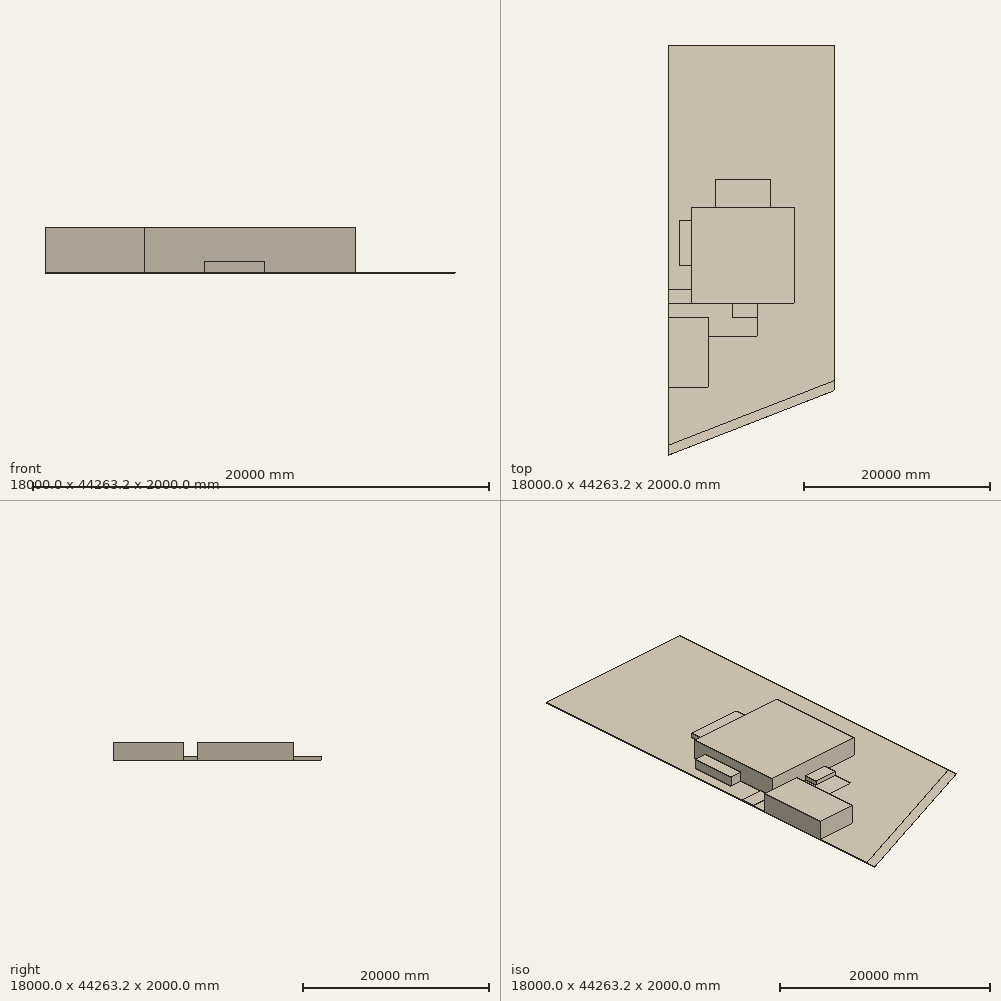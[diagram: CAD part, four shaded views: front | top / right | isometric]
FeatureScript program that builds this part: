
annotation { "Feature Type Name" : "Feature", "Feature Type Description" : "" }
export const myFeature = defineFeature(function(context is Context, id is Id, definition is map)
    precondition{}
    {
        {
            var Q0;
            Q0=qCreatedBy(makeId("Top.planeOp"),FACE);
            var sketch = newSketch(context, id + "F0", { "sketchPlane" : qUnion([Q0])});
            skLineSegment(sketch, "E0", {"start": v(0, 0) * mm, "end": v(18000, 0) * mm});
            skLineSegment(sketch, "E1", {"start": v(18000, 0) * mm, "end": v(18000, -37248.55) * mm});
            skLineSegment(sketch, "E2", {"start": v(0, 0) * mm, "end": v(0, -44263.25) * mm});
            skLineSegment(sketch, "E3", {"start": v(0, -44263.25) * mm, "end": v(18000, -37248.55) * mm});
            skLineSegment(sketch, "E4.bottom", {"start": v(2500, -17500) * mm, "end": v(13600, -17500) * mm});
            skLineSegment(sketch, "E4.top", {"start": v(2500, -27890) * mm, "end": v(13600, -27890) * mm});
            skLineSegment(sketch, "E4.left", {"start": v(2500, -17500) * mm, "end": v(2500, -27890) * mm});
            skLineSegment(sketch, "E4.right", {"start": v(13600, -17500) * mm, "end": v(13600, -27890) * mm});
            skLineSegment(sketch, "E5.bottom", {"start": v(4360, -29390) * mm, "end": v(0, -29390) * mm});
            skLineSegment(sketch, "E5.top", {"start": v(4360, -36890) * mm, "end": v(0, -36890) * mm});
            skLineSegment(sketch, "E5.left", {"start": v(4360, -29390) * mm, "end": v(4360, -36890) * mm});
            skLineSegment(sketch, "E5.right", {"start": v(0, -29390) * mm, "end": v(0, -36890) * mm});
            skLineSegment(sketch, "E6", {"start": v(0, -43190) * mm, "end": v(18000, -36175.3) * mm});
            skLineSegment(sketch, "E7", {"start": v(13600, -27890) * mm, "end": v(13600, -37890) * mm, "construction": true});
            skSolve(sketch);
        }
        {
            var Q0;
            {var subQ1=sQuery(id+"F0.wireOp",EDGE,"E0");Q0=makeQuery(id+"F0.imprint","IMPRINT",FACE,{"disambiguationData":[TD([[makeQuery(id+"F0.imprint","IMPRINT",EDGE,{"derivedFrom":subQ1}),-1.0]])]});}
            var sketch = newSketch(context, id + "F1", { "sketchPlane" : qUnion([Q0])});
            skLineSegment(sketch, "E8", {"start": v(0, 0) * mm, "end": v(18000, 0) * mm});
            skLineSegment(sketch, "E9", {"start": v(18000, 0) * mm, "end": v(18000, -37248.55) * mm});
            skLineSegment(sketch, "E10", {"start": v(18000, -37248.55) * mm, "end": v(0, -44263.25) * mm});
            skLineSegment(sketch, "E11", {"start": v(0, -44263.25) * mm, "end": v(0, 0) * mm});
            skSolve(sketch);
        }
        {
            var Q0;
            {var subQ1=sQuery(id+"F1.wireOp",EDGE,"E8");Q0=makeQuery(id+"F1.imprint","IMPRINT",FACE,{"disambiguationData":[TD([[makeQuery(id+"F1.imprint","IMPRINT",EDGE,{"derivedFrom":subQ1}),-1.0]])]});}
            var sketch = newSketch(context, id + "F2", { "sketchPlane" : qUnion([Q0])});
            skLineSegment(sketch, "E12.bottom", {"start": v(7000, -27890) * mm, "end": v(9600, -27890) * mm});
            skLineSegment(sketch, "E12.top", {"start": v(7000, -29340) * mm, "end": v(9600, -29340) * mm});
            skLineSegment(sketch, "E12.left", {"start": v(7000, -27890) * mm, "end": v(7000, -29340) * mm});
            skLineSegment(sketch, "E12.right", {"start": v(9600, -27890) * mm, "end": v(9600, -29340) * mm});
            skLineSegment(sketch, "E13", {"start": v(8300, -17500) * mm, "end": v(8300, -27890) * mm, "construction": true});
            skLineSegment(sketch, "E14", {"start": v(5660, -42057.52) * mm, "end": v(5660, -36890) * mm});
            skLineSegment(sketch, "E15.bottom", {"start": v(5086.7, -17500) * mm, "end": v(11086.7, -17500) * mm});
            skLineSegment(sketch, "E15.top", {"start": v(5086.7, -14500) * mm, "end": v(11086.7, -14500) * mm});
            skLineSegment(sketch, "E15.left", {"start": v(5086.7, -17500) * mm, "end": v(5086.7, -14500) * mm});
            skLineSegment(sketch, "E15.right", {"start": v(11086.7, -17500) * mm, "end": v(11086.7, -14500) * mm});
            skLineSegment(sketch, "E16", {"start": v(5660, -42057.52) * mm, "end": v(0, -44263.25) * mm});
            skLineSegment(sketch, "E17", {"start": v(0, -44263.25) * mm, "end": v(0, -36890) * mm});
            skLineSegment(sketch, "E18", {"start": v(0, -36890) * mm, "end": v(4360, -36890) * mm});
            skLineSegment(sketch, "E19", {"start": v(4360, -36890) * mm, "end": v(4360, -29390) * mm});
            skLineSegment(sketch, "E20", {"start": v(4360, -29390) * mm, "end": v(0, -29390) * mm});
            skLineSegment(sketch, "E21", {"start": v(0, -29390) * mm, "end": v(0, -26390) * mm});
            skLineSegment(sketch, "E22", {"start": v(0, -26390) * mm, "end": v(2500, -26390) * mm});
            skLineSegment(sketch, "E23", {"start": v(2500, -26390) * mm, "end": v(2500, -27890) * mm});
            skLineSegment(sketch, "E24", {"start": v(2500, -27890) * mm, "end": v(9600, -27890) * mm});
            skLineSegment(sketch, "E25", {"start": v(4360, -36890) * mm, "end": v(5660, -36890) * mm});
            skLineSegment(sketch, "E26", {"start": v(4360, -31390) * mm, "end": v(9600, -31390) * mm});
            skLineSegment(sketch, "E27", {"start": v(9600, -31390) * mm, "end": v(9600, -29340) * mm});
            skSolve(sketch);
        }
        {
            var Q0;
            {var subQ0=sQuery(id+"F2.wireOp",EDGE,"E18");Q0=makeQuery(id+"F2.imprint","IMPRINT",FACE,{"disambiguationData":[TD([[makeQuery(id+"F2.imprint","IMPRINT",EDGE,{"derivedFrom":subQ0}),1.0]])]});}
            extrude(context, id + "F3", {"entities" : qUnion([Q0]), "depth" : 25 * mm, "offsetDistance" : 25 * mm});
        }
        {
            var Q0;
            {var subQ1=sQuery(id+"F1.wireOp",EDGE,"E8");Q0=makeQuery(id+"F1.imprint","IMPRINT",FACE,{"disambiguationData":[TD([[makeQuery(id+"F1.imprint","IMPRINT",EDGE,{"derivedFrom":subQ1}),-1.0]])]});}
            extrude(context, id + "F4", {"entities" : qUnion([Q0]), "depth" : 25 * mm, "offsetDistance" : 25 * mm});
        }
        {
            var Q0;
            {var subQ0=sQuery(id+"F0.wireOp",EDGE,"E3");Q0=makeQuery(id+"F0.imprint","IMPRINT",FACE,{"disambiguationData":[TD([[makeQuery(id+"F0.imprint","IMPRINT",EDGE,{"derivedFrom":subQ0}),1.0]])]});}
            extrude(context, id + "F5", {"entities" : qUnion([Q0]), "operationType" : NewBodyOperationType.ADD, "depth" : 10 * mm, "offsetDistance" : 25 * mm});
        }
        {
            var Q0;
            Q0=makeQuery(id+"F0.imprint","IMPRINT",FACE,{"disambiguationData":[TD([[makeQuery(id+"F0.imprint","IMPRINT",EDGE,{"derivedFrom":sQuery(id+"F0.wireOp",EDGE,"E4.bottom")}),-1.0]])]});
            var Q1;
            Q1=makeQuery(id+"F0.imprint","IMPRINT",FACE,{"disambiguationData":[TD([[makeQuery(id+"F0.imprint","IMPRINT",EDGE,{"derivedFrom":sQuery(id+"F0.wireOp",EDGE,"E5.bottom")}),1.0]])]});
            extrude(context, id + "F6", {"entities" : qUnion([Q0, Q1]), "operationType" : NewBodyOperationType.ADD, "depth" : 2000 * mm, "offsetDistance" : 25 * mm});
        }
        {
            var Q0;
            Q0=makeQuery(id+"F2.imprint","IMPRINT",FACE,{"disambiguationData":[TD([[makeQuery(id+"F2.imprint","IMPRINT",EDGE,{"derivedFrom":sQuery(id+"F2.wireOp",EDGE,"E12.top")}),1.0]])]});
            var Q1;
            Q1=makeQuery(id+"F2.imprint","IMPRINT",FACE,{"disambiguationData":[TD([[makeQuery(id+"F2.imprint","IMPRINT",EDGE,{"derivedFrom":sQuery(id+"F2.wireOp",EDGE,"E15.bottom")}),1.0]])]});
            extrude(context, id + "F7", {"entities" : qUnion([Q0, Q1]), "operationType" : NewBodyOperationType.ADD, "depth" : 500 * mm, "offsetDistance" : 25 * mm});
        }
        {
            var Q0;
            Q0=makeQuery(id+"F2.imprint","IMPRINT",FACE,{"disambiguationData":[TD([[makeQuery(id+"F2.imprint","IMPRINT",EDGE,{"derivedFrom":sQuery(id+"F2.wireOp",EDGE,"E12.top")}),-1.0]])]});
            extrude(context, id + "F8", {"entities" : qUnion([Q0]), "operationType" : NewBodyOperationType.ADD, "depth" : 50 * mm, "offsetDistance" : 25 * mm});
        }
        {
            var Q0;
            Q0=makeQuery(id+"F8.opExtrude","CAP_FACE",FACE,{"disambiguationData":[OSD([sQuery(id+"F0.wireOp",EDGE,"E6"),sQuery(id+"F2.wireOp",EDGE,"E12.top"),sQuery(id+"F2.wireOp",EDGE,"E12.left"),sQuery(id+"F2.wireOp",EDGE,"E12.right"),sQuery(id+"F2.wireOp",EDGE,"E14"),sQuery(id+"F2.wireOp",EDGE,"XaijlOeH-sqg7-ABXU-oAYc-w8q2kSdBYU4V"),sQuery(id+"F2.wireOp",EDGE,"E17"),sQuery(id+"F2.wireOp",EDGE,"E18"),sQuery(id+"F2.wireOp",EDGE,"E19"),sQuery(id+"F2.wireOp",EDGE,"E20"),sQuery(id+"F2.wireOp",EDGE,"E21"),sQuery(id+"F2.wireOp",EDGE,"E22"),sQuery(id+"F2.wireOp",EDGE,"E23"),sQuery(id+"F2.wireOp",EDGE,"E24")])],"isStart":false});
            var sketch = newSketch(context, id + "F9", { "sketchPlane" : qUnion([Q0])});
            skLineSegment(sketch, "E28.bottom", {"start": v(2500, -27890) * mm, "end": v(0, -27890) * mm});
            skLineSegment(sketch, "E28.top", {"start": v(2500, -26390) * mm, "end": v(0, -26390) * mm});
            skLineSegment(sketch, "E28.left", {"start": v(2500, -27890) * mm, "end": v(2500, -26390) * mm});
            skLineSegment(sketch, "E28.right", {"start": v(0, -27890) * mm, "end": v(0, -26390) * mm});
            skSolve(sketch);
        }
        {
            var Q0;
            Q0 = qSketchRegion(id + "F9", true);
            extrude(context, id + "F10", {"entities" : qUnion([Q0]), "operationType" : NewBodyOperationType.ADD, "depth" : 25 * mm, "offsetDistance" : 25 * mm});
        }
        {
            var Q0;
            Q0=qCreatedBy(makeId("Top.planeOp"),FACE);
            var sketch = newSketch(context, id + "F11", { "sketchPlane" : qUnion([Q0])});
            skLineSegment(sketch, "E29.bottom", {"start": v(2500, -18900) * mm, "end": v(1200, -18900) * mm});
            skLineSegment(sketch, "E29.top", {"start": v(2500, -23700) * mm, "end": v(1200, -23700) * mm});
            skLineSegment(sketch, "E29.left", {"start": v(2500, -18900) * mm, "end": v(2500, -23700) * mm});
            skLineSegment(sketch, "E29.right", {"start": v(1200, -18900) * mm, "end": v(1200, -23700) * mm});
            skSolve(sketch);
        }
        {
            var Q0;
            Q0 = qSketchRegion(id + "F11", true);
            extrude(context, id + "F12", {"entities" : qUnion([Q0]), "operationType" : NewBodyOperationType.ADD, "depth" : 1000 * mm, "offsetDistance" : 25 * mm});
        }
    });
